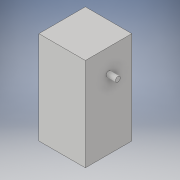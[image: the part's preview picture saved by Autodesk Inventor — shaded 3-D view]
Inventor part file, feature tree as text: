
AUTODESK INVENTOR PART (.ipt)
format: ipt  version: 2019 (Build 230136000, 136)  size: 100,352 bytes
history: native  units: mm
features: extrude x2, sketch x2, other x1
ambient origin geometry x8: Origin, YZ Plane, XZ Plane, XY Plane, X Axis, Y Axis, Z Axis, Center Point
bodies: Body1 (feature_tree)
feature tree (5):
  other  "Твердое тело1"
  extrude  "Выдавливание1"  Depth=40.0mm
  extrude  "Выдавливание2"  Depth=20.0mm
  sketch  "Эскиз1"
  sketch  "Эскиз2"
